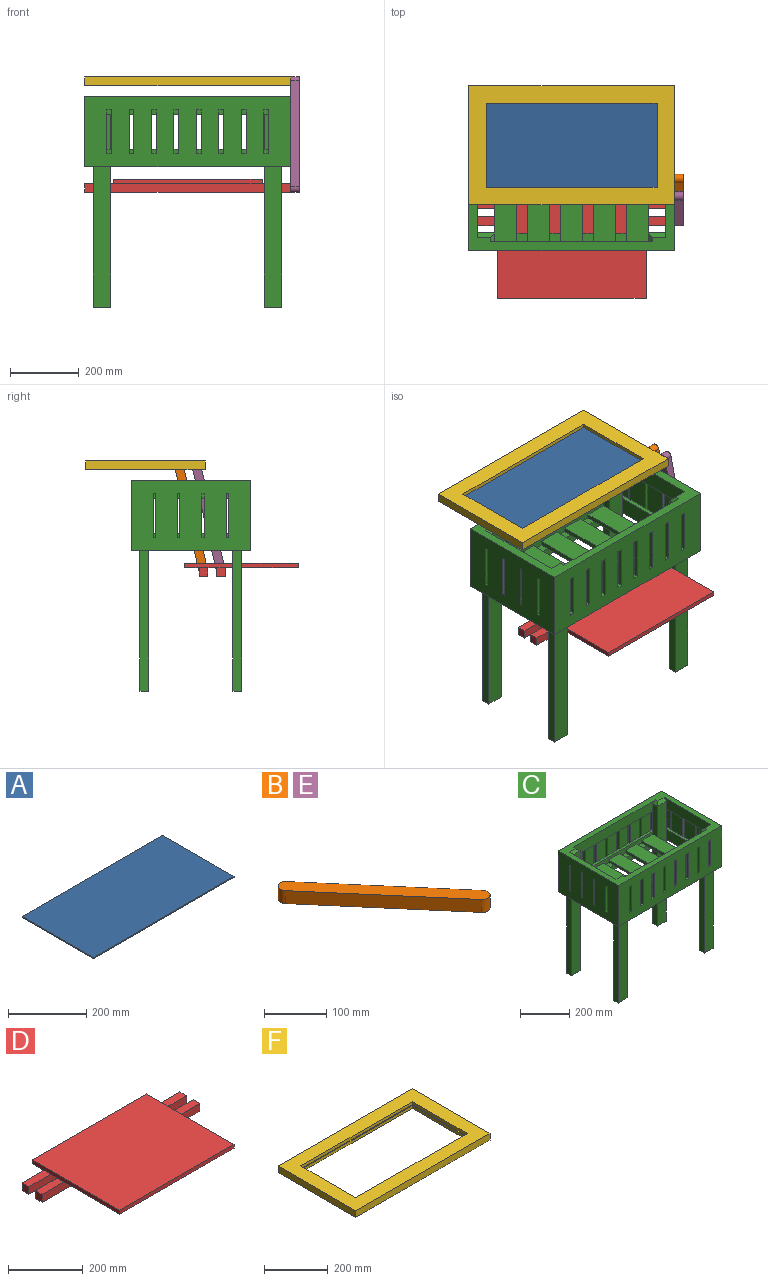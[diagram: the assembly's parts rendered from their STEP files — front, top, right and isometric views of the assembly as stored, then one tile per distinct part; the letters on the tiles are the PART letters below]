
ASSEMBLY  parts=6 mates=7
PART A: 6 faces, bbox 508x257.2x3.2 mm
  f0: plane 257.18x3.18mm, normal (1,0,0), area 816.5mm2, adj f1,f3,f4,f5
  f1: plane 508x3.18mm, normal (0,1,0), area 1612.9mm2, adj f0,f2,f4,f5
  f2: plane 257.18x3.18mm, normal (-1,0,0), area 816.5mm2, adj f1,f3,f4,f5
  f3: plane 508x3.18mm, normal (0,-1,0), area 1612.9mm2, adj f0,f2,f4,f5
  f4: plane 508x257.18mm, normal (0,0,1), area 130644.9mm2, adj f0,f1,f2,f3
  f5: plane 508x257.18mm, normal (0,0,-1), area 130644.9mm2, adj f0,f1,f2,f3
PART B: 6 faces, bbox 231.8x266.7x25.4 mm
  f0: plane 241.3x206.38mm, normal (0.76,0.65,0), area 8064.9mm2, adj f1,f3,f4,f5
  f1: cylinder r=12.7mm len=25.4mm, axis (0,0,-1), area 1013.4mm2, adj f0,f2,f4,f5
  f2: plane 241.3x206.38mm, normal (-0.76,-0.65,0), area 8064.9mm2, adj f1,f3,f4,f5
  f3: cylinder r=12.7mm len=25.4mm, axis (0,0,-1), area 1013.4mm2, adj f0,f2,f4,f5
  f4: plane 266.7x231.78mm, normal (0,0,1), area 8571.6mm2, adj f0,f1,f2,f3
  f5: plane 266.7x231.78mm, normal (0,0,-1), area 8571.6mm2, adj f0,f1,f2,f3
PART C: 254 faces, bbox 596.9x346.1x609.6 mm
  f0: plane 12.7x7.14mm, normal (0,0,1), area 90.7mm2, adj f4,f95,f250,f253
  f1: plane 12.7x7.14mm, normal (1,0,0), area 90.7mm2, adj f2,f125,f250,f253
  f2: plane 12.7x7.14mm, normal (0,0,-1), area 90.7mm2, adj f1,f95,f250,f253
  f3: plane 12.7x7.14mm, normal (0,0,1), area 90.7mm2, adj f8,f95,f247,f251
  f4: plane 12.7x7.14mm, normal (1,0,0), area 90.7mm2, adj f0,f99,f250,f253
  f5: plane 12.7x7.14mm, normal (1,0,0), area 90.7mm2, adj f6,f125,f247,f251
  f6: plane 12.7x7.14mm, normal (0,0,-1), area 90.7mm2, adj f5,f95,f247,f251
  f7: plane 12.7x7.14mm, normal (0,0,1), area 90.7mm2, adj f12,f95,f244,f248
  f8: plane 12.7x7.14mm, normal (1,0,0), area 90.7mm2, adj f3,f99,f247,f251
  f9: plane 12.7x7.14mm, normal (1,0,0), area 90.7mm2, adj f10,f125,f244,f248
  f10: plane 12.7x7.14mm, normal (0,0,-1), area 90.7mm2, adj f9,f95,f244,f248
  f11: plane 12.7x7.14mm, normal (0,0,1), area 90.7mm2, adj f15,f95,f241,f245
  f12: plane 12.7x7.14mm, normal (1,0,0), area 90.7mm2, adj f7,f99,f244,f248
  f13: plane 12.7x7.14mm, normal (1,0,0), area 90.7mm2, adj f14,f125,f241,f245
  f14: plane 12.7x7.14mm, normal (0,0,-1), area 90.7mm2, adj f13,f95,f241,f245
  f15: plane 12.7x7.14mm, normal (1,0,0), area 90.7mm2, adj f11,f99,f241,f245
  f16: plane 12.7x7.14mm, normal (0,0,-1), area 90.7mm2, adj f17,f97,f237,f240
  f17: plane 12.7x7.14mm, normal (-1,0,0), area 90.7mm2, adj f16,f125,f237,f240
  f18: plane 12.7x7.14mm, normal (0,0,1), area 90.7mm2, adj f20,f97,f237,f240
  f19: plane 12.7x7.14mm, normal (0,0,-1), area 90.7mm2, adj f21,f97,f234,f238
  f20: plane 12.7x7.14mm, normal (-1,0,0), area 90.7mm2, adj f18,f99,f237,f240
  f21: plane 12.7x7.14mm, normal (-1,0,0), area 90.7mm2, adj f19,f125,f234,f238
  f22: plane 12.7x7.14mm, normal (0,0,1), area 90.7mm2, adj f24,f97,f234,f238
  f23: plane 12.7x7.14mm, normal (0,0,-1), area 90.7mm2, adj f25,f97,f231,f235
  f24: plane 12.7x7.14mm, normal (-1,0,0), area 90.7mm2, adj f22,f99,f234,f238
  f25: plane 12.7x7.14mm, normal (-1,0,0), area 90.7mm2, adj f23,f125,f231,f235
  f26: plane 12.7x7.14mm, normal (0,0,1), area 90.7mm2, adj f28,f97,f231,f235
  f27: plane 12.7x7.14mm, normal (0,0,-1), area 90.7mm2, adj f29,f97,f228,f232
  f28: plane 12.7x7.14mm, normal (-1,0,0), area 90.7mm2, adj f26,f99,f231,f235
  f29: plane 12.7x7.14mm, normal (-1,0,0), area 90.7mm2, adj f27,f125,f228,f232
  f30: plane 12.7x7.14mm, normal (0,0,1), area 90.7mm2, adj f31,f97,f228,f232
  f31: plane 12.7x7.14mm, normal (-1,0,0), area 90.7mm2, adj f30,f99,f228,f232
  f32: plane 14.29x12.7mm, normal (0,0,1), area 181.5mm2, adj f33,f96,f224,f227
  f33: plane 14.29x12.7mm, normal (0,1,0), area 181.5mm2, adj f32,f99,f224,f227
  f34: plane 14.29x12.7mm, normal (0,1,0), area 181.5mm2, adj f35,f125,f224,f227
  f35: plane 14.29x12.7mm, normal (0,0,-1), area 181.5mm2, adj f34,f96,f224,f227
  f36: plane 14.29x12.7mm, normal (0,0,1), area 181.5mm2, adj f37,f96,f221,f225
  f37: plane 14.29x12.7mm, normal (0,1,0), area 181.5mm2, adj f36,f99,f221,f225
  f38: plane 14.29x12.7mm, normal (0,1,0), area 181.5mm2, adj f39,f125,f221,f225
  f39: plane 14.29x12.7mm, normal (0,0,-1), area 181.5mm2, adj f38,f96,f221,f225
  f40: plane 14.29x12.7mm, normal (0,0,1), area 181.5mm2, adj f41,f96,f218,f222
  f41: plane 14.29x12.7mm, normal (0,1,0), area 181.5mm2, adj f40,f99,f218,f222
  f42: plane 14.29x12.7mm, normal (0,1,0), area 181.5mm2, adj f43,f125,f218,f222
  f43: plane 14.29x12.7mm, normal (0,0,-1), area 181.5mm2, adj f42,f96,f218,f222
  f44: plane 14.29x12.7mm, normal (0,0,1), area 181.5mm2, adj f45,f96,f215,f219
  f45: plane 14.29x12.7mm, normal (0,1,0), area 181.5mm2, adj f44,f99,f215,f219
  f46: plane 14.29x12.7mm, normal (0,1,0), area 181.5mm2, adj f47,f125,f215,f219
  f47: plane 14.29x12.7mm, normal (0,0,-1), area 181.5mm2, adj f46,f96,f215,f219
  f48: plane 14.29x12.7mm, normal (0,0,1), area 181.5mm2, adj f49,f96,f212,f216
  f49: plane 14.29x12.7mm, normal (0,1,0), area 181.5mm2, adj f48,f99,f212,f216
  f50: plane 14.29x12.7mm, normal (0,1,0), area 181.5mm2, adj f51,f125,f212,f216
  f51: plane 14.29x12.7mm, normal (0,0,-1), area 181.5mm2, adj f50,f96,f212,f216
  f52: plane 14.29x12.7mm, normal (0,0,1), area 181.5mm2, adj f53,f96,f209,f213
  f53: plane 14.29x12.7mm, normal (0,1,0), area 181.5mm2, adj f52,f99,f209,f213
  f54: plane 14.29x12.7mm, normal (0,1,0), area 181.5mm2, adj f55,f125,f209,f213
  f55: plane 14.29x12.7mm, normal (0,0,-1), area 181.5mm2, adj f54,f96,f209,f213
  f56: plane 14.29x12.7mm, normal (0,0,1), area 181.5mm2, adj f57,f96,f206,f210
  f57: plane 14.29x12.7mm, normal (0,1,0), area 181.5mm2, adj f56,f99,f206,f210
  f58: plane 14.29x12.7mm, normal (0,1,0), area 181.5mm2, adj f59,f125,f206,f210
  f59: plane 14.29x12.7mm, normal (0,0,-1), area 181.5mm2, adj f58,f96,f206,f210
  f60: plane 14.29x12.7mm, normal (0,0,1), area 181.5mm2, adj f61,f96,f204,f207
  f61: plane 14.29x12.7mm, normal (0,1,0), area 181.5mm2, adj f60,f99,f204,f207
  f62: plane 14.29x12.7mm, normal (0,1,0), area 181.5mm2, adj f63,f125,f204,f207
  f63: plane 14.29x12.7mm, normal (0,0,-1), area 181.5mm2, adj f62,f96,f204,f207
  f64: plane 14.29x12.7mm, normal (0,-1,0), area 181.5mm2, adj f67,f99,f200,f202
  f65: plane 14.29x12.7mm, normal (0,0,-1), area 181.5mm2, adj f66,f98,f200,f202
  f66: plane 14.29x12.7mm, normal (0,-1,0), area 181.5mm2, adj f65,f125,f200,f202
  f67: plane 14.29x12.7mm, normal (0,0,1), area 181.5mm2, adj f64,f98,f200,f202
  f68: plane 14.29x12.7mm, normal (0,-1,0), area 181.5mm2, adj f71,f99,f197,f199
  f69: plane 14.29x12.7mm, normal (0,0,-1), area 181.5mm2, adj f70,f98,f197,f199
  f70: plane 14.29x12.7mm, normal (0,-1,0), area 181.5mm2, adj f69,f125,f197,f199
  f71: plane 14.29x12.7mm, normal (0,0,1), area 181.5mm2, adj f68,f98,f197,f199
  f72: plane 14.29x12.7mm, normal (0,-1,0), area 181.5mm2, adj f75,f99,f194,f196
  f73: plane 14.29x12.7mm, normal (0,0,-1), area 181.5mm2, adj f74,f98,f194,f196
  f74: plane 14.29x12.7mm, normal (0,-1,0), area 181.5mm2, adj f73,f125,f194,f196
  f75: plane 14.29x12.7mm, normal (0,0,1), area 181.5mm2, adj f72,f98,f194,f196
  f76: plane 14.29x12.7mm, normal (0,-1,0), area 181.5mm2, adj f79,f99,f191,f193
  f77: plane 14.29x12.7mm, normal (0,0,-1), area 181.5mm2, adj f78,f98,f191,f193
  f78: plane 14.29x12.7mm, normal (0,-1,0), area 181.5mm2, adj f77,f125,f191,f193
  f79: plane 14.29x12.7mm, normal (0,0,1), area 181.5mm2, adj f76,f98,f191,f193
  f80: plane 14.29x12.7mm, normal (0,-1,0), area 181.5mm2, adj f83,f99,f188,f190
  f81: plane 14.29x12.7mm, normal (0,0,-1), area 181.5mm2, adj f82,f98,f188,f190
  f82: plane 14.29x12.7mm, normal (0,-1,0), area 181.5mm2, adj f81,f125,f188,f190
  f83: plane 14.29x12.7mm, normal (0,0,1), area 181.5mm2, adj f80,f98,f188,f190
  f84: plane 14.29x12.7mm, normal (0,-1,0), area 181.5mm2, adj f87,f99,f185,f187
  f85: plane 14.29x12.7mm, normal (0,0,-1), area 181.5mm2, adj f86,f98,f185,f187
  f86: plane 14.29x12.7mm, normal (0,-1,0), area 181.5mm2, adj f85,f125,f185,f187
  f87: plane 14.29x12.7mm, normal (0,0,1), area 181.5mm2, adj f84,f98,f185,f187
  f88: plane 14.29x12.7mm, normal (0,-1,0), area 181.5mm2, adj f92,f99,f182,f184
  f89: plane 14.29x12.7mm, normal (0,0,-1), area 181.5mm2, adj f90,f98,f182,f184
  f90: plane 14.29x12.7mm, normal (0,-1,0), area 181.5mm2, adj f89,f125,f182,f184
  f91: plane 14.29x12.7mm, normal (0,-1,0), area 181.5mm2, adj f99,f177,f179,f181
  f92: plane 14.29x12.7mm, normal (0,0,1), area 181.5mm2, adj f88,f98,f182,f184
  f93: plane 14.29x12.7mm, normal (0,0,-1), area 181.5mm2, adj f94,f98,f179,f181
  f94: plane 14.29x12.7mm, normal (0,-1,0), area 181.5mm2, adj f93,f125,f179,f181
  f95: plane 346.08x203.2mm, normal (1,0,0), area 66693.4mm2, adj f0,f2,f3,f6,f7,f10,f11,f14
  f96: plane 596.9x203.2mm, normal (0,1,0), area 106774mm2, adj f32,f35,f36,f39,f40,f43,f44,f47
  f97: plane 346.08x203.2mm, normal (-1,0,0), area 66693.4mm2, adj f16,f18,f19,f22,f23,f26,f27,f30
  f98: plane 596.9x203.2mm, normal (0,-1,0), area 106774mm2, adj f65,f67,f69,f71,f73,f75,f77,f79
  f99: plane 571.5x320.68mm, normal (0,0,1), area 22016.1mm2, adj f4,f8,f12,f15,f20,f24,f28,f31
  f100: plane 152.4x25.4mm, normal (-1,0,0), area 3871mm2, adj f123,f128,f129,f146,f168,f172
  f101: plane 31.75x25.4mm, normal (0,0,1), area 806.5mm2, adj f129,f146,f162,f167
  f102: plane 31.75x25.4mm, normal (0,0,1), area 806.5mm2, adj f103,f134,f162,f167
  f103: plane 444.5x25.4mm, normal (0,1,0), area 7258mm2, adj f99,f102,f105,f107,f110,f111,f112,f151
  f104: plane 31.75x25.4mm, normal (0,0,1), area 806.5mm2, adj f129,f146,f158,f163
  f105: plane 31.75x25.4mm, normal (0,0,1), area 806.4mm2, adj f103,f134,f158,f163
  f106: plane 31.75x25.4mm, normal (0,0,1), area 806.5mm2, adj f129,f146,f154,f159
  f107: plane 31.75x25.4mm, normal (0,0,1), area 806.4mm2, adj f103,f134,f154,f159
  f108: plane 152.4x25.4mm, normal (1,0,0), area 3871mm2, adj f123,f129,f138,f146,f152,f174
  f109: plane 31.75x25.4mm, normal (0,0,1), area 806.5mm2, adj f129,f146,f151,f155
  f110: plane 31.75x25.4mm, normal (0,0,1), area 806.5mm2, adj f103,f134,f151,f155
  f111: plane 152.4x25.4mm, normal (-1,0,0), area 3871mm2, adj f103,f121,f133,f134,f168,f170
  f112: plane 152.4x25.4mm, normal (1,0,0), area 3871mm2, adj f103,f121,f134,f142,f152,f176
  f113: plane 406.4x25.4mm, normal (1,0,0), area 10322.6mm2, adj f114,f129,f131,f148
  f114: plane 406.4x50.8mm, normal (0,1,0), area 20645.1mm2, adj f113,f130,f131,f148
  f115: plane 406.4x25.4mm, normal (1,0,0), area 10322.6mm2, adj f116,f134,f136,f148
  f116: plane 406.4x50.8mm, normal (0,-1,0), area 20645.1mm2, adj f115,f135,f136,f148
  f117: plane 406.4x25.4mm, normal (-1,0,0), area 10322.6mm2, adj f118,f129,f140,f148
  f118: plane 406.4x50.8mm, normal (0,1,0), area 20645.1mm2, adj f117,f139,f140,f148
  f119: plane 406.4x25.4mm, normal (-1,0,0), area 10322.6mm2, adj f120,f134,f144,f148
  f120: plane 406.4x50.8mm, normal (0,-1,0), area 20645.1mm2, adj f119,f143,f144,f148
  f121: plane 469.9x50.8mm, normal (0,1,0), area 22741.9mm2, adj f111,f112,f125,f126,f170,f176
  f122: plane 269.88x50.8mm, normal (1,0,0), area 12580.6mm2, adj f125,f126,f129,f134,f173,f175
  f123: plane 469.9x50.8mm, normal (0,-1,0), area 22741.9mm2, adj f100,f108,f125,f126,f172,f174
  f124: plane 269.88x50.8mm, normal (-1,0,0), area 12580.6mm2, adj f125,f126,f129,f134,f169,f171
  f125: plane 571.5x320.68mm, normal (0,0,-1), area 22016.1mm2, adj f1,f5,f9,f13,f17,f21,f25,f29
  f126: plane 596.9x346.08mm, normal (0,0,1), area 47258mm2, adj f95,f96,f97,f98,f121,f122,f123,f124
  f127: plane 101.6x25.4mm, normal (1,0,0), area 2580.6mm2, adj f99,f125,f128,f129
  f128: plane 101.6x50.8mm, normal (0,1,0), area 5161.3mm2, adj f99,f100,f125,f127
  f129: plane 596.9x546.1mm, normal (0,-1,0), area 71935.3mm2, adj f100,f101,f104,f106,f108,f109,f113,f117
  f130: plane 406.4x25.4mm, normal (-1,0,0), area 10322.6mm2, adj f114,f129,f131,f148
  f131: plane 50.8x25.4mm, normal (0,0,-1), area 1290.3mm2, adj f113,f114,f129,f130
  f132: plane 101.6x25.4mm, normal (1,0,0), area 2580.6mm2, adj f99,f125,f133,f134
  f133: plane 101.6x50.8mm, normal (0,-1,0), area 5161.3mm2, adj f99,f111,f125,f132
  f134: plane 596.9x546.1mm, normal (0,1,0), area 71935.3mm2, adj f102,f105,f107,f110,f111,f112,f115,f119
  f135: plane 406.4x25.4mm, normal (-1,0,0), area 10322.6mm2, adj f116,f134,f136,f148
  f136: plane 50.8x25.4mm, normal (0,0,-1), area 1290.3mm2, adj f115,f116,f134,f135
  f137: plane 101.6x25.4mm, normal (-1,0,0), area 2580.6mm2, adj f99,f125,f129,f138
  f138: plane 101.6x50.8mm, normal (0,1,0), area 5161.3mm2, adj f99,f108,f125,f137
  f139: plane 406.4x25.4mm, normal (1,0,0), area 10322.6mm2, adj f118,f129,f140,f148
  f140: plane 50.8x25.4mm, normal (0,0,-1), area 1290.3mm2, adj f117,f118,f129,f139
  f141: plane 101.6x25.4mm, normal (-1,0,0), area 2580.6mm2, adj f99,f125,f134,f142
  f142: plane 101.6x50.8mm, normal (0,-1,0), area 5161.3mm2, adj f99,f112,f125,f141
  f143: plane 406.4x25.4mm, normal (1,0,0), area 10322.6mm2, adj f120,f134,f144,f148
  f144: plane 50.8x25.4mm, normal (0,0,-1), area 1290.3mm2, adj f119,f120,f134,f143
  f145: plane 244.48x50.8mm, normal (-1,0,0), area 12419.3mm2, adj f99,f129,f134,f148
  f146: plane 444.5x25.4mm, normal (0,-1,0), area 7258mm2, adj f99,f100,f101,f104,f106,f108,f109,f151
  f147: plane 244.48x50.8mm, normal (1,0,0), area 12419.3mm2, adj f99,f129,f134,f148
  f148: plane 596.9x346.08mm, normal (0,0,-1), area 67903.1mm2, adj f95,f96,f97,f98,f113,f114,f115,f116
  f149: plane 244.48x12.7mm, normal (-1,0,0), area 3104.8mm2, adj f129,f134,f150,f152
  f150: plane 244.48x63.5mm, normal (0,0,-1), area 15524.2mm2, adj f129,f134,f149,f151
  f151: plane 295.28x12.7mm, normal (1,0,0), area 3750mm2, adj f103,f109,f110,f146,f150,f152
  f152: plane 295.28x63.5mm, normal (0,0,1), area 18750mm2, adj f103,f108,f112,f146,f149,f151
  f153: plane 244.48x63.5mm, normal (0,0,-1), area 15524.2mm2, adj f129,f134,f154,f155
  f154: plane 295.28x12.7mm, normal (1,0,0), area 3750mm2, adj f103,f106,f107,f146,f153,f156
  f155: plane 295.28x12.7mm, normal (-1,0,0), area 3750mm2, adj f103,f109,f110,f146,f153,f156
  f156: plane 295.28x63.5mm, normal (0,0,1), area 18750mm2, adj f103,f146,f154,f155
  f157: plane 244.48x63.5mm, normal (0,0,-1), area 15524.2mm2, adj f129,f134,f158,f159
  f158: plane 295.28x12.7mm, normal (1,0,0), area 3750mm2, adj f103,f104,f105,f146,f157,f160
  f159: plane 295.28x12.7mm, normal (-1,0,0), area 3750mm2, adj f103,f106,f107,f146,f157,f160
  f160: plane 295.28x63.5mm, normal (0,0,1), area 18750mm2, adj f103,f146,f158,f159
  f161: plane 244.48x63.5mm, normal (0,0,-1), area 15524.2mm2, adj f129,f134,f162,f163
  f162: plane 295.28x12.7mm, normal (1,0,0), area 3750mm2, adj f101,f102,f103,f146,f161,f164
  f163: plane 295.28x12.7mm, normal (-1,0,0), area 3750mm2, adj f103,f104,f105,f146,f161,f164
  f164: plane 295.28x63.5mm, normal (0,0,1), area 18750mm2, adj f103,f146,f162,f163
  f165: plane 244.48x12.7mm, normal (1,0,0), area 3104.8mm2, adj f129,f134,f166,f168
  f166: plane 244.48x63.5mm, normal (0,0,-1), area 15524.2mm2, adj f129,f134,f165,f167
  f167: plane 295.28x12.7mm, normal (-1,0,0), area 3750mm2, adj f101,f102,f103,f146,f166,f168
  f168: plane 295.28x63.5mm, normal (0,0,1), area 18750mm2, adj f100,f103,f111,f146,f165,f167
  f169: plane 50.8x12.7mm, normal (0,0.71,0.71), area 798.3mm2, adj f124,f126,f134,f170
  f170: plane 25.4x12.7mm, normal (-0.71,0,0.71), area 342.1mm2, adj f111,f121,f126,f169
  f171: plane 50.8x12.7mm, normal (0,-0.71,0.71), area 798.3mm2, adj f124,f126,f129,f172
  f172: plane 25.4x12.7mm, normal (-0.71,0,0.71), area 342.1mm2, adj f100,f123,f126,f171
  f173: plane 50.8x12.7mm, normal (0,-0.71,0.71), area 798.3mm2, adj f122,f126,f129,f174
  f174: plane 25.4x12.7mm, normal (0.71,0,0.71), area 342.1mm2, adj f108,f123,f126,f173
  f175: plane 50.8x12.7mm, normal (0,0.71,0.71), area 798.3mm2, adj f122,f126,f134,f176
  f176: plane 25.4x12.7mm, normal (0.71,0,0.71), area 342.1mm2, adj f112,f121,f126,f175
  f177: plane 14.29x12.7mm, normal (0,0,1), area 181.5mm2, adj f91,f98,f179,f181
  f178: plane 101.6x50.8mm, normal (0,1,0), area 5161.3mm2, adj f99,f125,f179,f239
  f179: plane 127x12.7mm, normal (1,0,0), area 1612.9mm2, adj f91,f93,f94,f98,f177,f178
  f180: plane 101.6x50.8mm, normal (0,1,0), area 5161.3mm2, adj f99,f125,f181,f182
  f181: plane 127x12.7mm, normal (-1,0,0), area 1612.9mm2, adj f91,f93,f94,f98,f177,f180
  f182: plane 127x12.7mm, normal (1,0,0), area 1612.9mm2, adj f88,f89,f90,f92,f98,f180
  f183: plane 101.6x50.8mm, normal (0,1,0), area 5161.3mm2, adj f99,f125,f184,f185
  f184: plane 127x12.7mm, normal (-1,0,0), area 1612.9mm2, adj f88,f89,f90,f92,f98,f183
  f185: plane 127x12.7mm, normal (1,0,0), area 1612.9mm2, adj f84,f85,f86,f87,f98,f183
  f186: plane 101.6x50.8mm, normal (0,1,0), area 5161.3mm2, adj f99,f125,f187,f188
  f187: plane 127x12.7mm, normal (-1,0,0), area 1612.9mm2, adj f84,f85,f86,f87,f98,f186
  f188: plane 127x12.7mm, normal (1,0,0), area 1612.9mm2, adj f80,f81,f82,f83,f98,f186
  f189: plane 101.6x50.8mm, normal (0,1,0), area 5161.3mm2, adj f99,f125,f190,f191
  f190: plane 127x12.7mm, normal (-1,0,0), area 1612.9mm2, adj f80,f81,f82,f83,f98,f189
  f191: plane 127x12.7mm, normal (1,0,0), area 1612.9mm2, adj f76,f77,f78,f79,f98,f189
  f192: plane 101.6x50.8mm, normal (0,1,0), area 5161.3mm2, adj f99,f125,f193,f194
  f193: plane 127x12.7mm, normal (-1,0,0), area 1612.9mm2, adj f76,f77,f78,f79,f98,f192
  f194: plane 127x12.7mm, normal (1,0,0), area 1612.9mm2, adj f72,f73,f74,f75,f98,f192
  f195: plane 101.6x50.8mm, normal (0,1,0), area 5161.3mm2, adj f99,f125,f196,f197
  f196: plane 127x12.7mm, normal (-1,0,0), area 1612.9mm2, adj f72,f73,f74,f75,f98,f195
  f197: plane 127x12.7mm, normal (1,0,0), area 1612.9mm2, adj f68,f69,f70,f71,f98,f195
  f198: plane 101.6x50.8mm, normal (0,1,0), area 5161.3mm2, adj f99,f125,f199,f200
  f199: plane 127x12.7mm, normal (-1,0,0), area 1612.9mm2, adj f68,f69,f70,f71,f98,f198
  f200: plane 127x12.7mm, normal (1,0,0), area 1612.9mm2, adj f64,f65,f66,f67,f98,f198
  f201: plane 101.6x50.8mm, normal (0,1,0), area 5161.3mm2, adj f99,f125,f202,f252
  f202: plane 127x12.7mm, normal (-1,0,0), area 1612.9mm2, adj f64,f65,f66,f67,f98,f201
  f203: plane 101.6x50.8mm, normal (0,-1,0), area 5161.3mm2, adj f99,f125,f204,f229
  f204: plane 127x12.7mm, normal (1,0,0), area 1612.9mm2, adj f60,f61,f62,f63,f96,f203
  f205: plane 101.6x50.8mm, normal (0,-1,0), area 5161.3mm2, adj f99,f125,f206,f207
  f206: plane 127x12.7mm, normal (1,0,0), area 1612.9mm2, adj f56,f57,f58,f59,f96,f205
  f207: plane 127x12.7mm, normal (-1,0,0), area 1612.9mm2, adj f60,f61,f62,f63,f96,f205
  f208: plane 101.6x50.8mm, normal (0,-1,0), area 5161.3mm2, adj f99,f125,f209,f210
  f209: plane 127x12.7mm, normal (1,0,0), area 1612.9mm2, adj f52,f53,f54,f55,f96,f208
  f210: plane 127x12.7mm, normal (-1,0,0), area 1612.9mm2, adj f56,f57,f58,f59,f96,f208
  f211: plane 101.6x50.8mm, normal (0,-1,0), area 5161.3mm2, adj f99,f125,f212,f213
  f212: plane 127x12.7mm, normal (1,0,0), area 1612.9mm2, adj f48,f49,f50,f51,f96,f211
  f213: plane 127x12.7mm, normal (-1,0,0), area 1612.9mm2, adj f52,f53,f54,f55,f96,f211
  f214: plane 101.6x50.8mm, normal (0,-1,0), area 5161.3mm2, adj f99,f125,f215,f216
  f215: plane 127x12.7mm, normal (1,0,0), area 1612.9mm2, adj f44,f45,f46,f47,f96,f214
  f216: plane 127x12.7mm, normal (-1,0,0), area 1612.9mm2, adj f48,f49,f50,f51,f96,f214
  f217: plane 101.6x50.8mm, normal (0,-1,0), area 5161.3mm2, adj f99,f125,f218,f219
  f218: plane 127x12.7mm, normal (1,0,0), area 1612.9mm2, adj f40,f41,f42,f43,f96,f217
  f219: plane 127x12.7mm, normal (-1,0,0), area 1612.9mm2, adj f44,f45,f46,f47,f96,f217
  f220: plane 101.6x50.8mm, normal (0,-1,0), area 5161.3mm2, adj f99,f125,f221,f222
  f221: plane 127x12.7mm, normal (1,0,0), area 1612.9mm2, adj f36,f37,f38,f39,f96,f220
  f222: plane 127x12.7mm, normal (-1,0,0), area 1612.9mm2, adj f40,f41,f42,f43,f96,f220
  f223: plane 101.6x50.8mm, normal (0,-1,0), area 5161.3mm2, adj f99,f125,f224,f225
  f224: plane 127x12.7mm, normal (1,0,0), area 1612.9mm2, adj f32,f33,f34,f35,f96,f223
  f225: plane 127x12.7mm, normal (-1,0,0), area 1612.9mm2, adj f36,f37,f38,f39,f96,f223
  f226: plane 101.6x50.8mm, normal (0,-1,0), area 5161.3mm2, adj f99,f125,f227,f242
  f227: plane 127x12.7mm, normal (-1,0,0), area 1612.9mm2, adj f32,f33,f34,f35,f96,f226
  f228: plane 127x12.7mm, normal (0,-1,0), area 1612.9mm2, adj f27,f29,f30,f31,f97,f229
  f229: plane 101.6x50.8mm, normal (1,0,0), area 5161.3mm2, adj f99,f125,f203,f228
  f230: plane 101.6x63.5mm, normal (1,0,0), area 6451.6mm2, adj f99,f125,f231,f232
  f231: plane 127x12.7mm, normal (0,-1,0), area 1612.9mm2, adj f23,f25,f26,f28,f97,f230
  f232: plane 127x12.7mm, normal (0,1,0), area 1612.9mm2, adj f27,f29,f30,f31,f97,f230
  f233: plane 101.6x63.5mm, normal (1,0,0), area 6451.6mm2, adj f99,f125,f234,f235
  f234: plane 127x12.7mm, normal (0,-1,0), area 1612.9mm2, adj f19,f21,f22,f24,f97,f233
  f235: plane 127x12.7mm, normal (0,1,0), area 1612.9mm2, adj f23,f25,f26,f28,f97,f233
  f236: plane 101.6x63.5mm, normal (1,0,0), area 6451.6mm2, adj f99,f125,f237,f238
  f237: plane 127x12.7mm, normal (0,-1,0), area 1612.9mm2, adj f16,f17,f18,f20,f97,f236
  f238: plane 127x12.7mm, normal (0,1,0), area 1612.9mm2, adj f19,f21,f22,f24,f97,f236
  f239: plane 101.6x50.8mm, normal (1,0,0), area 5161.3mm2, adj f99,f125,f178,f240
  f240: plane 127x12.7mm, normal (0,1,0), area 1612.9mm2, adj f16,f17,f18,f20,f97,f239
  f241: plane 127x12.7mm, normal (0,-1,0), area 1612.9mm2, adj f11,f13,f14,f15,f95,f242
  f242: plane 101.6x50.8mm, normal (-1,0,0), area 5161.3mm2, adj f99,f125,f226,f241
  f243: plane 101.6x63.5mm, normal (-1,0,0), area 6451.6mm2, adj f99,f125,f244,f245
  f244: plane 127x12.7mm, normal (0,-1,0), area 1612.9mm2, adj f7,f9,f10,f12,f95,f243
  f245: plane 127x12.7mm, normal (0,1,0), area 1612.9mm2, adj f11,f13,f14,f15,f95,f243
  f246: plane 101.6x63.5mm, normal (-1,0,0), area 6451.6mm2, adj f99,f125,f247,f248
  f247: plane 127x12.7mm, normal (0,-1,0), area 1612.9mm2, adj f3,f5,f6,f8,f95,f246
  f248: plane 127x12.7mm, normal (0,1,0), area 1612.9mm2, adj f7,f9,f10,f12,f95,f246
  f249: plane 101.6x63.5mm, normal (-1,0,0), area 6451.6mm2, adj f99,f125,f250,f251
  f250: plane 127x12.7mm, normal (0,-1,0), area 1612.9mm2, adj f0,f1,f2,f4,f95,f249
  f251: plane 127x12.7mm, normal (0,1,0), area 1612.9mm2, adj f3,f5,f6,f8,f95,f249
  f252: plane 101.6x50.8mm, normal (-1,0,0), area 5161.3mm2, adj f99,f125,f201,f253
  f253: plane 127x12.7mm, normal (0,1,0), area 1612.9mm2, adj f0,f1,f2,f4,f95,f252
PART D: 22 faces, bbox 596.9x330.2x38.1 mm
  f0: plane 431.8x211.14mm, normal (0,0,-1), area 91169.2mm2, adj f2,f4,f5,f18
  f1: plane 431.8x25.4mm, normal (0,0,-1), area 10967.7mm2, adj f2,f4,f11,f16
  f2: plane 330.2x12.7mm, normal (1,0,0), area 4193.5mm2, adj f0,f1,f3,f5,f6,f7,f8,f15
  f3: plane 431.8x12.7mm, normal (0,1,0), area 5483.9mm2, adj f2,f4,f6,f7
  f4: plane 330.2x12.7mm, normal (-1,0,0), area 4193.5mm2, adj f0,f1,f3,f5,f6,f7,f10,f17
  f5: plane 431.8x12.7mm, normal (0,-1,0), area 5483.9mm2, adj f0,f2,f4,f7
  f6: plane 431.8x42.86mm, normal (0,0,-1), area 18508mm2, adj f2,f3,f4,f9
  f7: plane 431.8x330.2mm, normal (0,0,1), area 142580.4mm2, adj f2,f3,f4,f5
  f8: plane 82.55x25.4mm, normal (0,0,1), area 2096.8mm2, adj f2,f9,f11,f13
  f9: plane 596.9x25.4mm, normal (0,1,0), area 15161.3mm2, adj f6,f8,f10,f12,f13,f14
  f10: plane 82.55x25.4mm, normal (0,0,1), area 2096.8mm2, adj f4,f9,f11,f14
  f11: plane 596.9x25.4mm, normal (0,-1,0), area 15161.3mm2, adj f1,f8,f10,f12,f13,f14
  f12: plane 596.9x25.4mm, normal (0,0,-1), area 15161.3mm2, adj f9,f11,f13,f14
  f13: plane 25.4x25.4mm, normal (1,0,0), area 645.2mm2, adj f8,f9,f11,f12
  f14: plane 25.4x25.4mm, normal (-1,0,0), area 645.2mm2, adj f9,f10,f11,f12
  f15: plane 82.55x25.4mm, normal (0,0,1), area 2096.8mm2, adj f2,f16,f18,f20
  f16: plane 596.9x25.4mm, normal (0,1,0), area 15161.3mm2, adj f1,f15,f17,f19,f20,f21
  f17: plane 82.55x25.4mm, normal (0,0,1), area 2096.8mm2, adj f4,f16,f18,f21
  f18: plane 596.9x25.4mm, normal (0,-1,0), area 15161.3mm2, adj f0,f15,f17,f19,f20,f21
  f19: plane 596.9x25.4mm, normal (0,0,-1), area 15161.3mm2, adj f16,f18,f20,f21
  f20: plane 25.4x25.4mm, normal (1,0,0), area 645.2mm2, adj f15,f16,f18,f19
  f21: plane 25.4x25.4mm, normal (-1,0,0), area 645.2mm2, adj f16,f17,f18,f19
PART E: same geometry as B
PART F: 20 faces, bbox 596.9x346.1x25.4 mm
  f0: plane 495.3x11.05mm, normal (0,-1,0), area 5472.6mm2, adj f1,f3,f13,f18
  f1: plane 244.48x11.05mm, normal (-1,0,0), area 2701.2mm2, adj f0,f2,f13,f18
  f2: plane 495.3x11.05mm, normal (0,1,0), area 5472.6mm2, adj f1,f3,f13,f18
  f3: plane 244.48x11.05mm, normal (1,0,0), area 2701.2mm2, adj f0,f2,f13,f18
  f4: plane 495.3x11.05mm, normal (0,-1,0), area 5472.6mm2, adj f5,f11,f12,f19
  f5: plane 244.48x11.05mm, normal (-1,0,0), area 2701.2mm2, adj f4,f6,f12,f19
  f6: plane 495.3x11.05mm, normal (0,1,0), area 5472.6mm2, adj f5,f11,f12,f19
  f7: plane 346.08x25.4mm, normal (1,0,0), area 8790.3mm2, adj f8,f10,f12,f13
  f8: plane 596.9x25.4mm, normal (0,1,0), area 15161.3mm2, adj f7,f9,f12,f13
  f9: plane 346.08x25.4mm, normal (-1,0,0), area 8790.3mm2, adj f8,f10,f12,f13
  f10: plane 596.9x25.4mm, normal (0,-1,0), area 15161.3mm2, adj f7,f9,f12,f13
  f11: plane 244.48x11.05mm, normal (1,0,0), area 2701.2mm2, adj f4,f6,f12,f19
  f12: plane 596.9x346.08mm, normal (0,0,1), area 85483.7mm2, adj f4,f5,f6,f7,f8,f9,f10,f11
  f13: plane 596.9x346.08mm, normal (0,0,-1), area 85483.7mm2, adj f0,f1,f2,f3,f7,f8,f9,f10
  f14: plane 257.18x3.3mm, normal (-1,0,0), area 849.2mm2, adj f15,f17,f18,f19
  f15: plane 508x3.3mm, normal (0,-1,0), area 1677.4mm2, adj f14,f16,f18,f19
  f16: plane 257.18x3.3mm, normal (1,0,0), area 849.2mm2, adj f15,f17,f18,f19
  f17: plane 508x3.3mm, normal (0,1,0), area 1677.4mm2, adj f14,f16,f18,f19
  f18: plane 508x257.18mm, normal (0,0,1), area 9556.4mm2, adj f0,f1,f2,f3,f14,f15,f16,f17
  f19: plane 508x257.18mm, normal (0,0,-1), area 9556.4mm2, adj f4,f5,f6,f11,f14,f15,f16,f17
PLACE A t=(0,131.84,43.3)mm
PLACE B rot(axis=(0.3,0.91,0.3),95.6deg) t=(298.45,35,44.89)mm
PLACE C at identity fixed
PLACE D rot(axis=(1,0,0),0deg) t=(0,-146.48,-35.77)mm
PLACE E rot(axis=(0.3,0.91,0.3),95.6deg) t=(298.45,-15.8,44.89)mm
PLACE F rot(axis=(-1,0,0),0deg) t=(0,131.84,32.19)mm
MATE fastened F.f15 <-> A.f1  axis (0,-1,0) through (0,260.42,44.89)mm
MATE revolute E.f3 <-> D.f20  axis (-1,0,0) through (298.45,-87.75,-264.37)mm
MATE revolute E.f1 <-> F.f7  axis (-1,0,0) through (298.45,-15.8,44.89)mm
MATE revolute B.f5 <-> C.f95  axis (-1,0,0) through (298.45,0.92,-101.6)mm
MATE revolute B.f1 <-> F.f7  axis (-1,0,0) through (298.45,35,44.89)mm
MATE revolute B.f3 <-> D.f13  axis (-1,0,0) through (298.45,-36.95,-264.37)mm
MATE revolute E.f5 <-> C.f95  axis (-1,0,0) through (298.45,-49.88,-101.6)mm
